SOLIDWORKS PART (.sldprt)
format: sldprt  version: not decoded by parser v0  size: 84,480 bytes
history: native  units: mm
features: sketch x5, plane x3, cut_extrude x3, extrude x2, material x1 (+10 scaffold rows collapsed)
feature tree (24):
  scaffold x10  (default folders/planes/origin — collapsed)
  material  "Matériau <non spécifié>"
  plane  "Plan de face"
  plane  "Plan de dessus"
  plane  "Plan de droite"
  sketch  "Esquisse1"  dims[D1=12.0mm]
  extrude  "Extrusion1"  Depth=6mm
  sketch  "Esquisse2"  dims[D1=10.5mm]
  extrude  "Extrusion2"  Depth=2mm
  sketch  "Esquisse3"  dims[D1=1.55mm]
  cut_extrude  "Enlèv. mat.-Extru.1"  [1 undecoded]
  sketch  "Esquisse4"  dims[D1=7.5mm]
  cut_extrude  "Enlèv. mat.-Extru.2"  [1 undecoded]
  sketch  "Esquisse5"  dims[D1=~0.796977mm]
  cut_extrude  "Enlèv. mat.-Extru.3"  Depth=10mm
decode coverage: 8 of 10 modeling features carry decoded parameters
note: ~ marks probable driven/reference dimensions
note: 2 parameter values undecoded
note: suppression state not decoded; provenance and decode notes live in map.json
